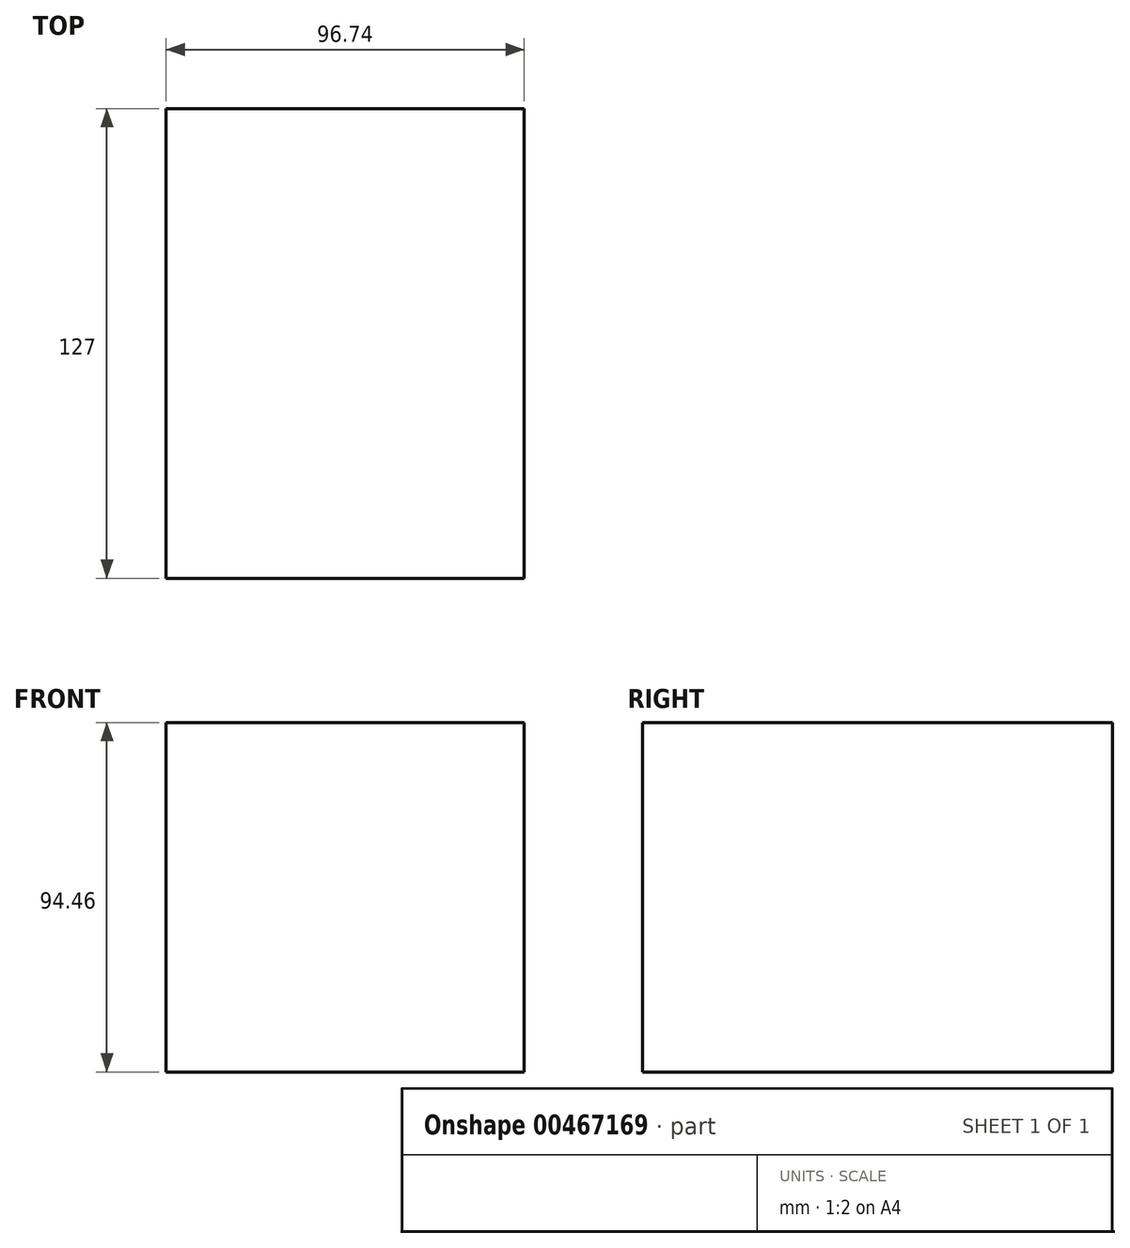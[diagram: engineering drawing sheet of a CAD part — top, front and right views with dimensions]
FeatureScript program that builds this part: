
annotation { "Feature Type Name" : "Feature", "Feature Type Description" : "" }
export const myFeature = defineFeature(function(context is Context, id is Id, definition is map)
    precondition{}
    {
        {
            var Q0;
            Q0=qCreatedBy(makeId("Front.planeOp"),FACE);
            var sketch = newSketch(context, id + "F0", { "sketchPlane" : qUnion([Q0])});
            skLineSegment(sketch, "E0.bottom", {"start": v(48.37, 47.23) * mm, "end": v(-48.37, 47.23) * mm});
            skLineSegment(sketch, "E0.top", {"start": v(48.37, -47.23) * mm, "end": v(-48.37, -47.23) * mm});
            skLineSegment(sketch, "E0.left", {"start": v(48.37, 47.23) * mm, "end": v(48.37, -47.23) * mm});
            skLineSegment(sketch, "E0.right", {"start": v(-48.37, 47.23) * mm, "end": v(-48.37, -47.23) * mm});
            skPoint(sketch, "E0.middle", {"position": v(0, 0) * mm});
            skSolve(sketch);
        }
        {
            var Q0;
            Q0 = qSketchRegion(id + "F0", true);
            extrude(context, id + "F1", {"entities" : qUnion([Q0]), "endBound" : BoundingType.SYMMETRIC, "depth" : 127 * mm});
        }
    });
